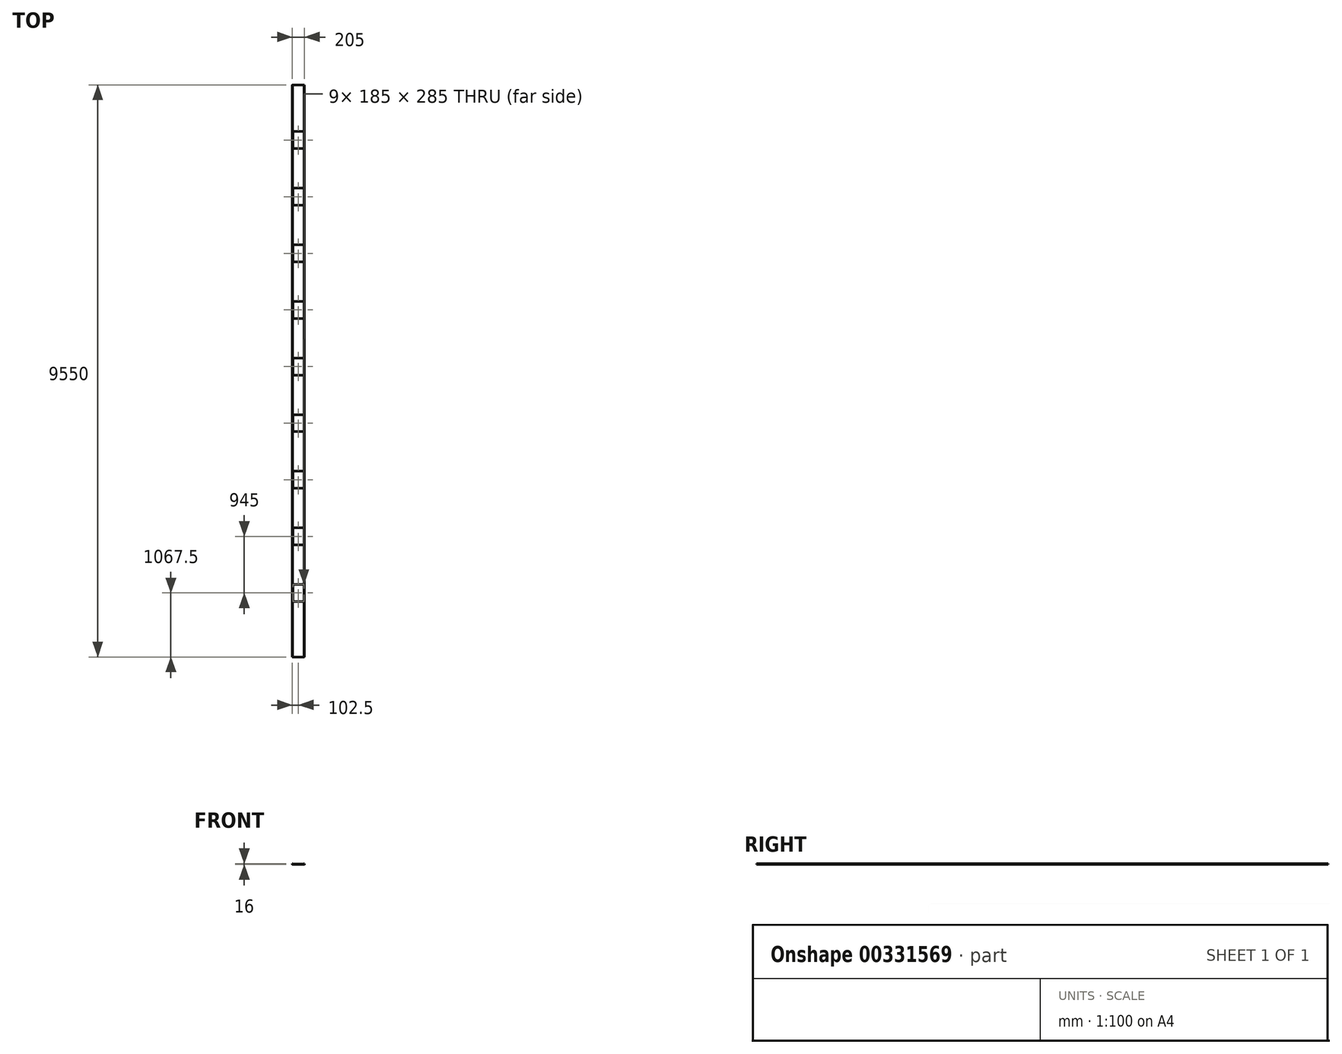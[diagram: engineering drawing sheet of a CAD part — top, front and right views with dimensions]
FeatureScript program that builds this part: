
annotation { "Feature Type Name" : "Feature", "Feature Type Description" : "" }
export const myFeature = defineFeature(function(context is Context, id is Id, definition is map)
    precondition{}
    {
        {
            var Q0;
            Q0=qCreatedBy(makeId("Front.planeOp"),FACE);
            var sketch = newSketch(context, id + "F0", { "sketchPlane" : qUnion([Q0])});
            skLineSegment(sketch, "E0.top", {"start": v(100, -16) * mm, "end": v(-100, -16) * mm});
            skLineSegment(sketch, "E0.left", {"start": v(102.5, 0) * mm, "end": v(102.5, -13.5) * mm});
            skLineSegment(sketch, "E0.right", {"start": v(-102.5, 0) * mm, "end": v(-102.5, -13.5) * mm});
            skPoint(sketch, "E0.middle", {"position": v(0, 0) * mm});
            skLineSegment(sketch, "E1.bottom", {"start": v(94, -10) * mm, "end": v(-94, -10) * mm});
            skLineSegment(sketch, "E1.left", {"start": v(96.5, -7.5) * mm, "end": v(96.5, 0) * mm});
            skLineSegment(sketch, "E1.right", {"start": v(-96.5, -7.5) * mm, "end": v(-96.5, 0) * mm});
            skLineSegment(sketch, "E2.bottom", {"start": v(97, -13) * mm, "end": v(-97, -13) * mm});
            skLineSegment(sketch, "E2.left", {"start": v(99.5, -10.5) * mm, "end": v(99.5, 0) * mm});
            skLineSegment(sketch, "E2.right", {"start": v(-99.5, -10.5) * mm, "end": v(-99.5, 0) * mm});
            skLineSegment(sketch, "E3", {"start": v(-102.5, 0) * mm, "end": v(-96.5, 0) * mm});
            skPoint(sketch, "E4.orphan", {"position": v(-99.5, 13) * mm});
            skPoint(sketch, "E0.bottom.end.orphan", {"position": v(-102.5, 16) * mm});
            skPoint(sketch, "E1.top.end.orphan", {"position": v(-96.5, 10) * mm});
            skPoint(sketch, "E5.orphan", {"position": v(96.5, 10) * mm});
            skPoint(sketch, "E6.orphan", {"position": v(99.5, 13) * mm});
            skPoint(sketch, "E7.orphan", {"position": v(102.5, 16) * mm});
            skLineSegment(sketch, "E8.trimOffspring", {"start": v(96.5, 0) * mm, "end": v(102.5, 0) * mm});
            skPoint(sketch, "E9.visualSharp", {"position": v(102.5, -16) * mm});
            skArc(sketch, "E9.filletArc", {"start": v(100, -16) * mm, "mid": v(101.77, -15.27) * mm, "end": v(102.5, -13.5) * mm});
            skPoint(sketch, "E10.visualSharp", {"position": v(96.5, -10) * mm});
            skArc(sketch, "E10.filletArc", {"start": v(94, -10) * mm, "mid": v(95.77, -9.27) * mm, "end": v(96.5, -7.5) * mm});
            skPoint(sketch, "E11.visualSharp", {"position": v(-96.5, -10) * mm});
            skArc(sketch, "E11.filletArc", {"start": v(-96.5, -7.5) * mm, "mid": v(-95.77, -9.27) * mm, "end": v(-94, -10) * mm});
            skPoint(sketch, "E12.visualSharp", {"position": v(-102.5, -16) * mm});
            skArc(sketch, "E12.filletArc", {"start": v(-102.5, -13.5) * mm, "mid": v(-101.77, -15.27) * mm, "end": v(-100, -16) * mm});
            skPoint(sketch, "E13.visualSharp", {"position": v(-99.5, -13) * mm});
            skArc(sketch, "E13.filletArc", {"start": v(-99.5, -10.5) * mm, "mid": v(-98.77, -12.27) * mm, "end": v(-97, -13) * mm});
            skPoint(sketch, "E14.visualSharp", {"position": v(99.5, -13) * mm});
            skArc(sketch, "E14.filletArc", {"start": v(97, -13) * mm, "mid": v(98.77, -12.27) * mm, "end": v(99.5, -10.5) * mm});
            skSolve(sketch);
        }
        {
            var Q0;
            Q0 = qSketchRegion(id + "F0", true);
            extrude(context, id + "F1", {"entities" : qUnion([Q0]), "depth" : 9550 * mm});
        }
        {
            var Q0;
            Q0=makeQuery(id+"F1.opExtrude","SWEPT_FACE",FACE,{"disambiguationData":[OSD([sQuery(id+"F0.wireOp",EDGE,"E1.bottom")])]});
            var sketch = newSketch(context, id + "F2", { "sketchPlane" : qUnion([Q0])});
            skLineSegment(sketch, "E15.bottom", {"start": v(-92.5, -8340) * mm, "end": v(92.5, -8340) * mm});
            skLineSegment(sketch, "E15.top", {"start": v(-92.5, -8625) * mm, "end": v(92.5, -8625) * mm});
            skLineSegment(sketch, "E15.left", {"start": v(-92.5, -8340) * mm, "end": v(-92.5, -8625) * mm});
            skLineSegment(sketch, "E15.right", {"start": v(92.5, -8340) * mm, "end": v(92.5, -8625) * mm});
            skPoint(sketch, "E15.middle", {"position": v(0, -8482.5) * mm});
            skLineSegment(sketch, "E16.bottom", {"start": v(-92.5, -7395) * mm, "end": v(92.5, -7395) * mm});
            skLineSegment(sketch, "E16.top", {"start": v(-92.5, -7680) * mm, "end": v(92.5, -7680) * mm});
            skLineSegment(sketch, "E16.left", {"start": v(-92.5, -7395) * mm, "end": v(-92.5, -7680) * mm});
            skLineSegment(sketch, "E16.right", {"start": v(92.5, -7395) * mm, "end": v(92.5, -7680) * mm});
            skPoint(sketch, "E16.middle", {"position": v(0, -7537.5) * mm});
            skLineSegment(sketch, "E17.bottom", {"start": v(-92.5, -6450) * mm, "end": v(92.5, -6450) * mm});
            skLineSegment(sketch, "E17.top", {"start": v(-92.5, -6735) * mm, "end": v(92.5, -6735) * mm});
            skLineSegment(sketch, "E17.left", {"start": v(-92.5, -6450) * mm, "end": v(-92.5, -6735) * mm});
            skLineSegment(sketch, "E17.right", {"start": v(92.5, -6450) * mm, "end": v(92.5, -6735) * mm});
            skPoint(sketch, "E17.middle", {"position": v(0, -6592.5) * mm});
            skLineSegment(sketch, "E18.bottom", {"start": v(-92.5, -5505) * mm, "end": v(92.5, -5505) * mm});
            skLineSegment(sketch, "E18.top", {"start": v(-92.5, -5790) * mm, "end": v(92.5, -5790) * mm});
            skLineSegment(sketch, "E18.left", {"start": v(-92.5, -5505) * mm, "end": v(-92.5, -5790) * mm});
            skLineSegment(sketch, "E18.right", {"start": v(92.5, -5505) * mm, "end": v(92.5, -5790) * mm});
            skPoint(sketch, "E18.middle", {"position": v(0, -5647.5) * mm});
            skLineSegment(sketch, "E19.bottom", {"start": v(-92.5, -4560) * mm, "end": v(92.5, -4560) * mm});
            skLineSegment(sketch, "E19.top", {"start": v(-92.5, -4845) * mm, "end": v(92.5, -4845) * mm});
            skLineSegment(sketch, "E19.left", {"start": v(-92.5, -4560) * mm, "end": v(-92.5, -4845) * mm});
            skLineSegment(sketch, "E19.right", {"start": v(92.5, -4560) * mm, "end": v(92.5, -4845) * mm});
            skPoint(sketch, "E19.middle", {"position": v(0, -4702.5) * mm});
            skLineSegment(sketch, "E20.bottom", {"start": v(-92.5, -3615) * mm, "end": v(92.5, -3615) * mm});
            skLineSegment(sketch, "E20.top", {"start": v(-92.5, -3900) * mm, "end": v(92.5, -3900) * mm});
            skLineSegment(sketch, "E20.left", {"start": v(-92.5, -3615) * mm, "end": v(-92.5, -3900) * mm});
            skLineSegment(sketch, "E20.right", {"start": v(92.5, -3615) * mm, "end": v(92.5, -3900) * mm});
            skPoint(sketch, "E20.middle", {"position": v(0, -3757.5) * mm});
            skLineSegment(sketch, "E21.bottom", {"start": v(-92.5, -2670) * mm, "end": v(92.5, -2670) * mm});
            skLineSegment(sketch, "E21.top", {"start": v(-92.5, -2955) * mm, "end": v(92.5, -2955) * mm});
            skLineSegment(sketch, "E21.left", {"start": v(-92.5, -2670) * mm, "end": v(-92.5, -2955) * mm});
            skLineSegment(sketch, "E21.right", {"start": v(92.5, -2670) * mm, "end": v(92.5, -2955) * mm});
            skPoint(sketch, "E21.middle", {"position": v(0, -2812.5) * mm});
            skLineSegment(sketch, "E22.bottom", {"start": v(-92.5, -1725) * mm, "end": v(92.5, -1725) * mm});
            skLineSegment(sketch, "E22.top", {"start": v(-92.5, -2010) * mm, "end": v(92.5, -2010) * mm});
            skLineSegment(sketch, "E22.left", {"start": v(-92.5, -1725) * mm, "end": v(-92.5, -2010) * mm});
            skLineSegment(sketch, "E22.right", {"start": v(92.5, -1725) * mm, "end": v(92.5, -2010) * mm});
            skPoint(sketch, "E22.middle", {"position": v(0, -1867.5) * mm});
            skLineSegment(sketch, "E23.bottom", {"start": v(-92.5, -780) * mm, "end": v(92.5, -780) * mm});
            skLineSegment(sketch, "E23.top", {"start": v(-92.5, -1065) * mm, "end": v(92.5, -1065) * mm});
            skLineSegment(sketch, "E23.left", {"start": v(-92.5, -780) * mm, "end": v(-92.5, -1065) * mm});
            skLineSegment(sketch, "E23.right", {"start": v(92.5, -780) * mm, "end": v(92.5, -1065) * mm});
            skPoint(sketch, "E23.middle", {"position": v(0, -922.5) * mm});
            skSolve(sketch);
        }
        {
            var Q0;
            Q0=makeQuery(id+"F2.imprint","IMPRINT",FACE,{"disambiguationData":[TD([[makeQuery(id+"F2.imprint","IMPRINT",EDGE,{"derivedFrom":sQuery(id+"F2.wireOp",EDGE,"E15.bottom")}),-1.0]])]});
            var Q1;
            Q1=makeQuery(id+"F2.imprint","IMPRINT",FACE,{"disambiguationData":[TD([[makeQuery(id+"F2.imprint","IMPRINT",EDGE,{"derivedFrom":sQuery(id+"F2.wireOp",EDGE,"E16.bottom")}),-1.0]])]});
            var Q2;
            Q2=makeQuery(id+"F2.imprint","IMPRINT",FACE,{"disambiguationData":[TD([[makeQuery(id+"F2.imprint","IMPRINT",EDGE,{"derivedFrom":sQuery(id+"F2.wireOp",EDGE,"E17.bottom")}),-1.0]])]});
            var Q3;
            Q3=makeQuery(id+"F2.imprint","IMPRINT",FACE,{"disambiguationData":[TD([[makeQuery(id+"F2.imprint","IMPRINT",EDGE,{"derivedFrom":sQuery(id+"F2.wireOp",EDGE,"E18.bottom")}),-1.0]])]});
            var Q4;
            Q4=makeQuery(id+"F2.imprint","IMPRINT",FACE,{"disambiguationData":[TD([[makeQuery(id+"F2.imprint","IMPRINT",EDGE,{"derivedFrom":sQuery(id+"F2.wireOp",EDGE,"E19.bottom")}),-1.0]])]});
            var Q5;
            Q5=makeQuery(id+"F2.imprint","IMPRINT",FACE,{"disambiguationData":[TD([[makeQuery(id+"F2.imprint","IMPRINT",EDGE,{"derivedFrom":sQuery(id+"F2.wireOp",EDGE,"E20.bottom")}),-1.0]])]});
            var Q6;
            Q6=makeQuery(id+"F2.imprint","IMPRINT",FACE,{"disambiguationData":[TD([[makeQuery(id+"F2.imprint","IMPRINT",EDGE,{"derivedFrom":sQuery(id+"F2.wireOp",EDGE,"E21.bottom")}),-1.0]])]});
            var Q7;
            Q7=makeQuery(id+"F2.imprint","IMPRINT",FACE,{"disambiguationData":[TD([[makeQuery(id+"F2.imprint","IMPRINT",EDGE,{"derivedFrom":sQuery(id+"F2.wireOp",EDGE,"E22.bottom")}),-1.0]])]});
            var Q8;
            Q8=makeQuery(id+"F2.imprint","IMPRINT",FACE,{"disambiguationData":[TD([[makeQuery(id+"F2.imprint","IMPRINT",EDGE,{"derivedFrom":sQuery(id+"F2.wireOp",EDGE,"E23.bottom")}),-1.0]])]});
            extrude(context, id + "F3", {"entities" : qUnion([Q0, Q1, Q2, Q3, Q4, Q5, Q6, Q7, Q8]), "operationType" : NewBodyOperationType.REMOVE, "oppositeDirection" : true, "depth" : 25 * mm});
        }
    });
